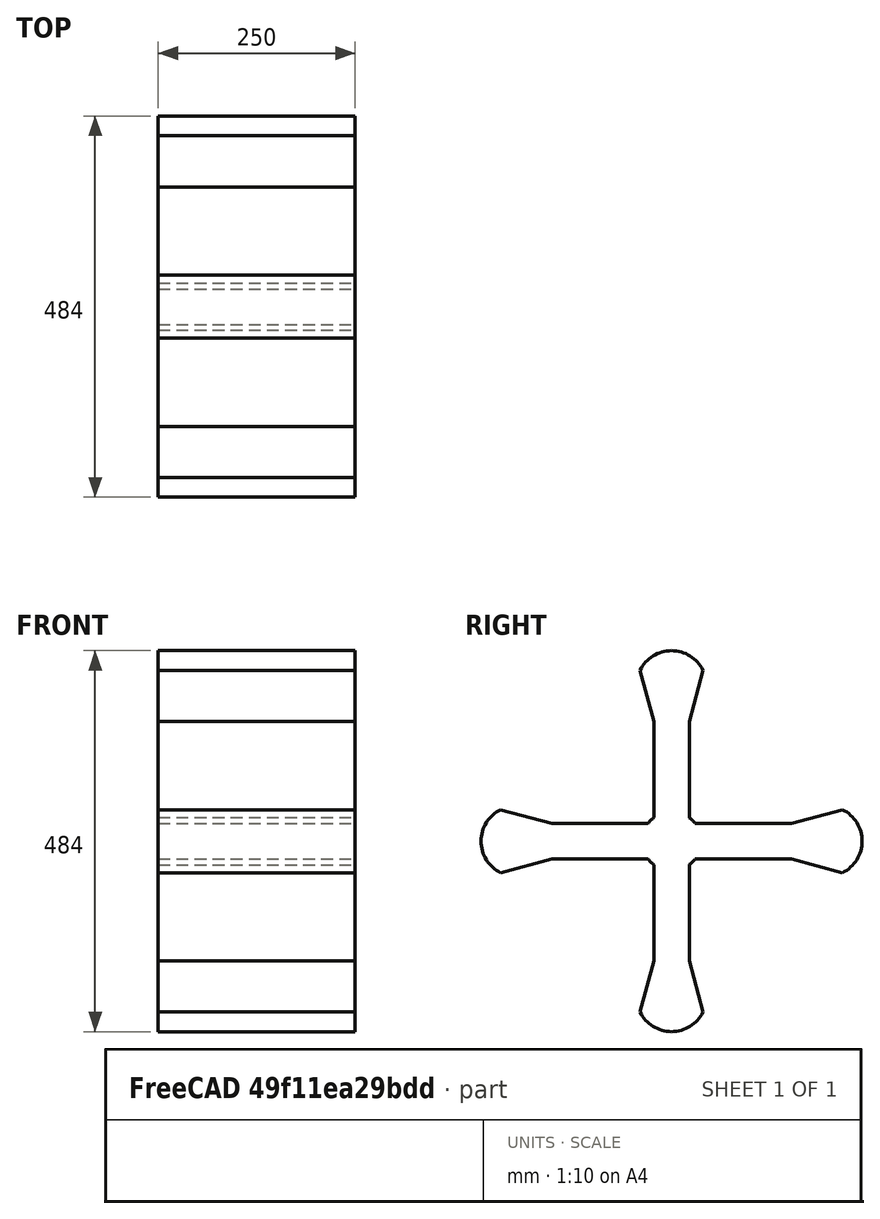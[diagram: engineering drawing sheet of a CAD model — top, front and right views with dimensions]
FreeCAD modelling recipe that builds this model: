
FCSTD DOCUMENT
Label: RotorProject
objects: Sketcher::SketchObject×1, PartDesign::Pad×1
note: 3 computed .brp shape members not serialized (recipe doc carries the construction recipe); baked Part::Feature solids carry a one-line shape summary decoded from their .brp

FEATURE [Sketcher::SketchObject] Sketch
  Placement = pos=(-125,0,0) rot=(0.57735,0.57735,0.57735;2.0944rad)
  sketch-geometry (33):
    g0: LineSegment StartX=-152 StartY=-22.5 StartZ=0 EndX=-217 EndY=-40.0019 EndZ=0
    g1: LineSegment [constr] StartX=-217 StartY=-40.0019 StartZ=0 EndX=-217 EndY=40.0019 EndZ=0
    g2: LineSegment StartX=-217 StartY=40.0019 StartZ=0 EndX=-152 EndY=22.5 EndZ=0
    g3: LineSegment StartX=-152 StartY=22.5 StartZ=0 EndX=-30 EndY=22.5 EndZ=0
    g4: LineSegment StartX=-152 StartY=-22.5 StartZ=0 EndX=-30 EndY=-22.5 EndZ=0
    g5: LineSegment StartX=-22.5 StartY=30 StartZ=0 EndX=-22.5 EndY=152 EndZ=0
    g6: LineSegment StartX=-22.5 StartY=152 StartZ=0 EndX=-40.0019 EndY=217 EndZ=0
    g7: LineSegment StartX=-22.5 StartY=-30 StartZ=0 EndX=-22.5 EndY=-152 EndZ=0
    g8: LineSegment StartX=-22.5 StartY=-152 StartZ=0 EndX=-40.0019 EndY=-217 EndZ=0
    g9: ArcOfCircle CenterX=0 CenterY=0 CenterZ=0 NormalX=0 NormalY=0 NormalZ=1 Radius=37.5 StartAngle=2.2143 EndAngle=2.49809
    g10: LineSegment StartX=40.0019 StartY=217 StartZ=0 EndX=22.5 EndY=152 EndZ=0
    g11: LineSegment StartX=22.5 StartY=152 StartZ=0 EndX=22.5 EndY=30 EndZ=0
    g12: LineSegment StartX=30.0014 StartY=22.4981 StartZ=0 EndX=152.001 EndY=22.4981 EndZ=0
    g13: LineSegment StartX=152.001 StartY=22.4981 StartZ=0 EndX=217.001 EndY=40 EndZ=0
    g14: LineSegment [constr] StartX=217.001 StartY=40 StartZ=0 EndX=217.001 EndY=-40 EndZ=0
    g15: LineSegment StartX=217.001 StartY=-40 StartZ=0 EndX=152.001 EndY=-22.4981 EndZ=0
    g16: LineSegment StartX=152.001 StartY=-22.4981 StartZ=0 EndX=30.0014 EndY=-22.4981 EndZ=0
    g17: LineSegment StartX=22.5 StartY=-30 StartZ=0 EndX=22.5 EndY=-152 EndZ=0
    g18: LineSegment StartX=22.5 StartY=-152 StartZ=0 EndX=40.0019 EndY=-217 EndZ=0
    g19: ArcOfCircle CenterX=0 CenterY=0 CenterZ=0 NormalX=0 NormalY=0 NormalZ=1 Radius=37.5 StartAngle=0.643439 EndAngle=0.927295
    g20: ArcOfCircle CenterX=0 CenterY=0 CenterZ=0 NormalX=0 NormalY=0 NormalZ=1 Radius=37.5 StartAngle=5.35589 EndAngle=5.63975
    g21: ArcOfCircle CenterX=0 CenterY=0 CenterZ=0 NormalX=0 NormalY=0 NormalZ=1 Radius=37.5 StartAngle=3.78509 EndAngle=4.06889
    g22: LineSegment [constr] StartX=-40.0019 StartY=217 StartZ=0 EndX=40.0019 EndY=217 EndZ=0
    g23: LineSegment [constr] StartX=-152 StartY=22.5 StartZ=0 EndX=-217 EndY=22.5 EndZ=0
    g24: ArcOfCircle CenterX=0 CenterY=197.497 CenterZ=0 NormalX=0 NormalY=0 NormalZ=1 Radius=44.503 StartAngle=0.453639 EndAngle=2.68795
    g25: ArcOfCircle CenterX=197.501 CenterY=0 CenterZ=0 NormalX=0 NormalY=0 NormalZ=1 Radius=44.5 StartAngle=5.16599 EndAngle=7.40038
    g26: ArcOfCircle CenterX=0 CenterY=-197.497 CenterZ=0 NormalX=0 NormalY=0 NormalZ=1 Radius=44.503 StartAngle=3.59523 EndAngle=5.82955
    g27: ArcOfCircle CenterX=-197.497 CenterY=0 CenterZ=0 NormalX=0 NormalY=0 NormalZ=1 Radius=44.503 StartAngle=2.02444 EndAngle=4.25875
    g28: LineSegment [constr] StartX=-242 StartY=0 StartZ=0 EndX=-217 EndY=0 EndZ=0
    g29: LineSegment [constr] StartX=0 StartY=242 StartZ=0 EndX=0 EndY=217 EndZ=0
    g30: LineSegment [constr] StartX=217.001 StartY=0 StartZ=0 EndX=242.001 EndY=0 EndZ=0
    g31: LineSegment [constr] StartX=-40.0019 StartY=-217 StartZ=0 EndX=40.0019 EndY=-217 EndZ=0
    g32: LineSegment [constr] StartX=0 StartY=-217 StartZ=0 EndX=0 EndY=-242 EndZ=0
  constraints (107):
    c: Coincident(g0,g1)
    c: Vertical(g1)
    c: Coincident(g1,g2)
    c: Coincident(g2,g3)
    c: Horizontal(g3)
    c: Coincident(g4,g0)
    c: Horizontal(g4)
    c: Vertical(g5)
    c: Coincident(g5,g6)
    c: Vertical(g7)
    c: Coincident(g8,g7)
    c: Equal(g3,g4)
    c: Equal(g4,g5)
    c: Equal(g5,g7)
    c: Equal(g6,g2)
    c: Equal(g2,g0)
    c: Equal(g0,g8)
    c: Coincident(g9,g3)
    c: Coincident(g9,g5)
    c: DistanceX(g9) = 0
    c: DistanceY(g9) = 0
    c: Radius(g9) = 37.5
    c: Coincident(g10,g11)
    c: Vertical(g11)
    c: Horizontal(g12)
    c: Coincident(g12,g13)
    c: Coincident(g13,g14)
    c: Vertical(g14)
    c: Coincident(g14,g15)
    c: Coincident(g15,g16)
    c: Horizontal(g16)
    c: Vertical(g17)
    c: Coincident(g17,g18)
    c: Coincident(g19,g11)
    c: Coincident(g19,g12)
    c: Coincident(g20,g16)
    c: Coincident(g20,g17)
    c: Equal(g12,g11)
    c: Equal(g11,g5)
    c: Equal(g5,g16)
    c: Equal(g16,g17)
    c: Equal(g13,g10)
    c: Equal(g10,g6)
    c: Equal(g6,g15)
    c: Equal(g15,g18)
    c: DistanceX(g19) = 0
    c: DistanceY(g19) = 0
    c: Coincident(g21,g4)
    c: Coincident(g21,g7)
    c: Equal(g9,g21)
    c: Equal(g21,g20)
    c: Equal(g20,g19)
    c: Coincident(g22,g6)
    c: Coincident(g22,g10)
    c: Horizontal(g22)
    c: Equal(g22,g1)
    c: DistanceX(g21) = 0
    c: DistanceY(g21) = 0
    c: DistanceX(g20) = 0
    c: DistanceY(g20) = 0
    c: Angle(g1,g2) = 1.30777
    c: Angle(g0,g1) = 1.30777
    c: Angle(g6,g22) = 1.30777
    c: Angle(g22,g10) = 1.30777
    c: Angle(g13,g14) = 1.30777
    c: Angle(g14,g15) = 1.30777
    c: Distance(g14) = 80
    c: Distance(g12) = 122
    c: PointOnObject(g23,g1)
    c: Coincident(g23,g2)
    c: Horizontal(g23)
    c: Distance(g23) = 65
    c: Coincident(g24,g6)
    c: Coincident(g24,g10)
    c: Coincident(g25,g13)
    c: Coincident(g25,g14)
    c: Coincident(g26,g8)
    c: Coincident(g26,g18)
    c: Coincident(g27,g0)
    c: Coincident(g27,g1)
    c: PointOnObject(g28,g27)
    c: PointOnObject(g28,g1)
    c: Horizontal(g28)
    c: Distance(g28) = 25
    c: PointOnObject(g29,g24)
    c: PointOnObject(g29,g22)
    c: Vertical(g29)
    c: Distance(g29) = 25
    c: PointOnObject(g30,g14)
    c: PointOnObject(g30,g25)
    c: Horizontal(g30)
    c: Distance(g30) = 25
    c: Coincident(g31,g8)
    c: Coincident(g31,g18)
    c: Horizontal(g31)
    c: PointOnObject(g32,g31)
    c: PointOnObject(g32,g26)
    c: Vertical(g32)
    c: Distance(g32) = 25
    c: Angle(g31,g8) = 1.30777
    c: Angle(g18,g31) = 1.30777
    c: DistanceY(g3) = 22.5
    c: DistanceX(g17) = 22.5
    c: DistanceY(g28) = 0
    c: DistanceY(g30) = 0
    c: DistanceX(g29) = 0
    c: DistanceX(g32) = 0
FEATURE [PartDesign::Pad] Pad
  Length = 250
  MirroredExtent = false
  Sketch = -> Sketch
